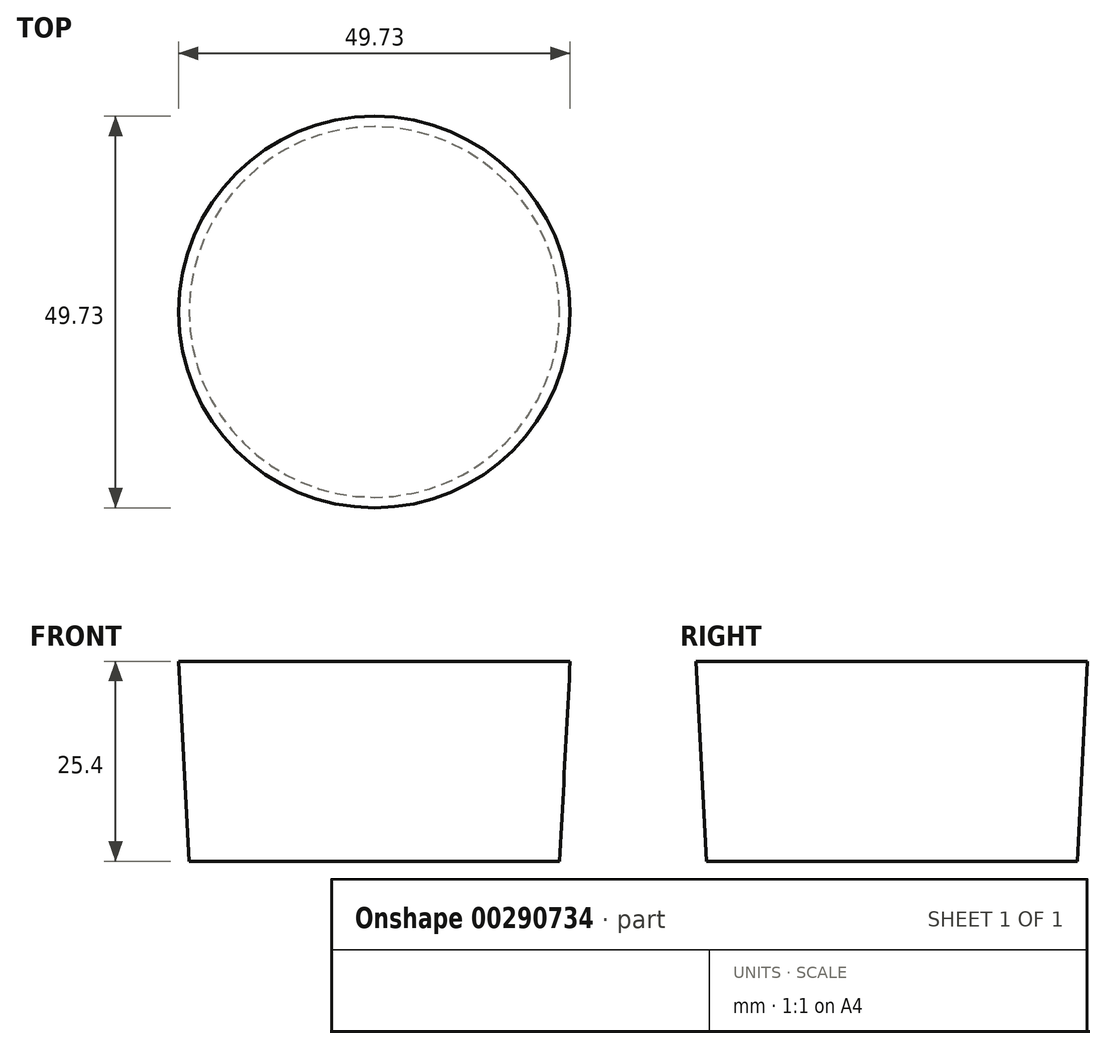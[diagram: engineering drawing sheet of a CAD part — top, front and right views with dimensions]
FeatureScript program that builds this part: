
annotation { "Feature Type Name" : "Feature", "Feature Type Description" : "" }
export const myFeature = defineFeature(function(context is Context, id is Id, definition is map)
    precondition{}
    {
        {
            var Q0;
            Q0=qCreatedBy(makeId("Top.planeOp"),FACE);
            var sketch = newSketch(context, id + "F0", { "sketchPlane" : qUnion([Q0])});
            skCircle(sketch, "E0", {"center": v(-42.67, 36.32) * mm, "radius": 23.53 * mm});
            skSolve(sketch);
        }
        {
            var Q0;
            Q0 = qSketchRegion(id + "F0", true);
            extrude(context, id + "F1", {"entities" : qUnion([Q0]), "depth" : 25.4 * mm, "hasDraft" : true, "draftAngle" : 3 * degree});
        }
    });
